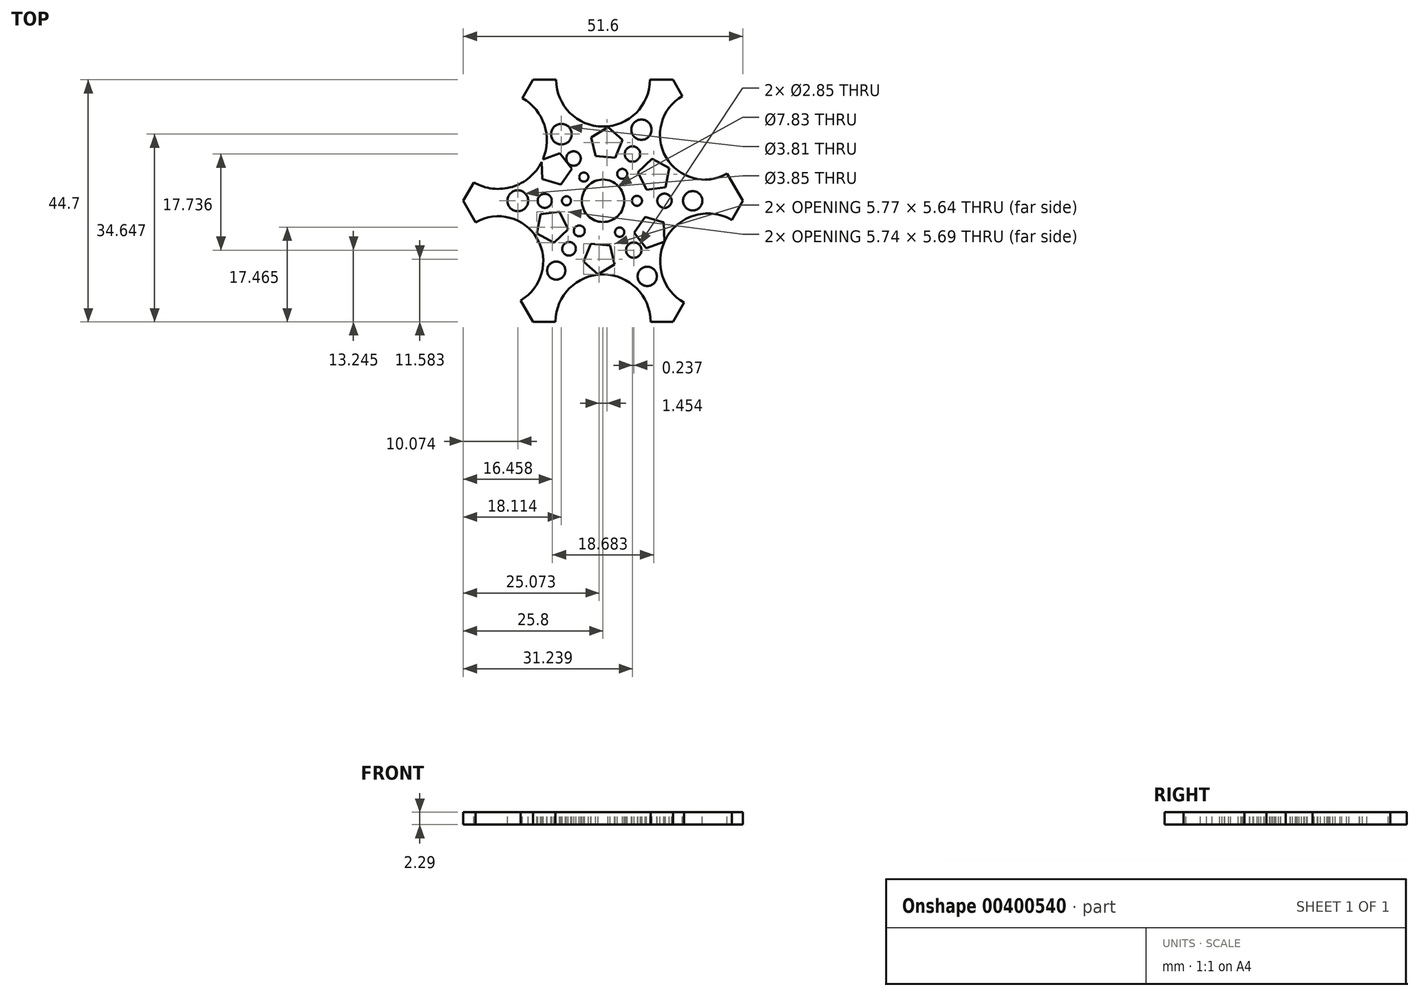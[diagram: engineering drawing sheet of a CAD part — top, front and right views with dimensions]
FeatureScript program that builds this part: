
annotation { "Feature Type Name" : "Feature", "Feature Type Description" : "" }
export const myFeature = defineFeature(function(context is Context, id is Id, definition is map)
    precondition{}
    {
        {
            var Q0;
            Q0=qCreatedBy(makeId("Top.planeOp"),FACE);
            var sketch = newSketch(context, id + "F0", { "sketchPlane" : qUnion([Q0])});
            skCircle(sketch, "E0.cCircle", {"center": v(0, 0) * mm, "radius": 37.25 * mm, "construction": true});
            skLineSegment(sketch, "E0.0", {"start": v(-21.5, 37.25) * mm, "end": v(21.5, 37.25) * mm});
            skLineSegment(sketch, "E0.1", {"start": v(21.5, 37.25) * mm, "end": v(43, 0) * mm});
            skLineSegment(sketch, "E0.2", {"start": v(43, 0) * mm, "end": v(21.5, -37.25) * mm});
            skLineSegment(sketch, "E0.3", {"start": v(21.5, -37.25) * mm, "end": v(-21.5, -37.25) * mm});
            skLineSegment(sketch, "E0.4", {"start": v(-21.5, -37.25) * mm, "end": v(-43, 0) * mm});
            skLineSegment(sketch, "E0.5", {"start": v(-43, 0) * mm, "end": v(-21.5, 37.25) * mm});
            skPoint(sketch, "E0.0.midPoint", {"position": v(0, 37.25) * mm});
            skSolve(sketch);
        }
        {
            var Q0;
            Q0 = qSketchRegion(id + "F0", true);
            extrude(context, id + "F1", {"entities" : qUnion([Q0]), "depth" : 3.8 * mm});
        }
        {
            var Q0;
            Q0=makeQuery(id+"F1.opExtrude","CAP_FACE",FACE,{"disambiguationData":[OSD([sQuery(id+"F0.wireOp",EDGE,"E0.0"),sQuery(id+"F0.wireOp",EDGE,"E0.1"),sQuery(id+"F0.wireOp",EDGE,"E0.2"),sQuery(id+"F0.wireOp",EDGE,"E0.3"),sQuery(id+"F0.wireOp",EDGE,"E0.4"),sQuery(id+"F0.wireOp",EDGE,"E0.5")])],"isStart":false});
            var sketch = newSketch(context, id + "F2", { "sketchPlane" : qUnion([Q0])});
            skCircle(sketch, "E1", {"center": v(0, 37.25) * mm, "radius": 14.42 * mm});
            skCircle(sketch, "E2", {"center": v(-32.26, 18.62) * mm, "radius": 14.97 * mm});
            skCircle(sketch, "E3", {"center": v(-32.26, -18.62) * mm, "radius": 13.87 * mm});
            skCircle(sketch, "E4", {"center": v(0, -37.25) * mm, "radius": 14.61 * mm});
            skCircle(sketch, "E5", {"center": v(32.26, -18.62) * mm, "radius": 14.69 * mm});
            skCircle(sketch, "E6", {"center": v(31.3, 20.28) * mm, "radius": 13.77 * mm});
            skCircle(sketch, "E7", {"center": v(0, 0) * mm, "radius": 6.53 * mm});
            skCircle(sketch, "E8", {"center": v(-12.8, 20.5) * mm, "radius": 3.18 * mm});
            skCircle(sketch, "E9", {"center": v(-9.07, 13) * mm, "radius": 2.23 * mm});
            skCircle(sketch, "E10", {"center": v(-5.91, 7.3) * mm, "radius": 1.4 * mm});
            skCircle(sketch, "E11", {"center": v(11.82, 21.87) * mm, "radius": 3.12 * mm});
            skCircle(sketch, "E12", {"center": v(9.07, 14.39) * mm, "radius": 2.37 * mm});
            skCircle(sketch, "E13", {"center": v(5.91, 8.28) * mm, "radius": 1.54 * mm});
            skCircle(sketch, "E14", {"center": v(27.59, 0) * mm, "radius": 2.96 * mm});
            skCircle(sketch, "E15", {"center": v(18.92, 0) * mm, "radius": 2.2 * mm});
            skCircle(sketch, "E16", {"center": v(13.6, -23.25) * mm, "radius": 2.96 * mm});
            skCircle(sketch, "E17", {"center": v(9.46, -15.17) * mm, "radius": 2.37 * mm});
            skCircle(sketch, "E18", {"center": v(5.12, -9.66) * mm, "radius": 1.43 * mm});
            skCircle(sketch, "E19", {"center": v(10.44, 0) * mm, "radius": 1.54 * mm});
            skCircle(sketch, "E20", {"center": v(-14.39, -21.48) * mm, "radius": 2.8 * mm});
            skCircle(sketch, "E21", {"center": v(-10.44, -14.78) * mm, "radius": 2.1 * mm});
            skCircle(sketch, "E22", {"center": v(-7.3, -9.26) * mm, "radius": 1.67 * mm});
            skCircle(sketch, "E23", {"center": v(-26.21, 0) * mm, "radius": 3.2 * mm});
            skCircle(sketch, "E24", {"center": v(-17.93, 0) * mm, "radius": 2.17 * mm});
            skCircle(sketch, "E25", {"center": v(-11.23, 0) * mm, "radius": 1.4 * mm});
            skSolve(sketch);
        }
        {
            var Q0;
            Q0 = qSketchRegion(id + "F2", true);
            extrude(context, id + "F3", {"entities" : qUnion([Q0]), "operationType" : NewBodyOperationType.REMOVE, "endBound" : BoundingType.THROUGH_ALL, "oppositeDirection" : true, "depth" : 25.4 * mm});
        }
        {
            var Q0;
            Q0=makeQuery(id+"F1.opExtrude","SWEPT_BODY",BODY,{"disambiguationData":[OSD([sQuery(id+"F0.wireOp",EDGE,"E0.0"),sQuery(id+"F0.wireOp",EDGE,"E0.1"),sQuery(id+"F0.wireOp",EDGE,"E0.2"),sQuery(id+"F0.wireOp",EDGE,"E0.3"),sQuery(id+"F0.wireOp",EDGE,"E0.4"),sQuery(id+"F0.wireOp",EDGE,"E0.5")])]});
            var Q1;
            Q1=qCreatedBy(makeId("Origin.pointOp"),VERTEX);
            transform(context, id + "F4", {"entities" : qUnion([Q0]), "transformType" : TransformType.SCALE_UNIFORMLY, "scale" : 0.6, "scalePoint" : qUnion([Q1]), "makeCopy" : false});
        }
        {
            var Q0;
            Q0=makeQuery(id+"F1.opExtrude","CAP_FACE",FACE,{"disambiguationData":[OSD([sQuery(id+"F0.wireOp",EDGE,"E0.0"),sQuery(id+"F0.wireOp",EDGE,"E0.1"),sQuery(id+"F0.wireOp",EDGE,"E0.2"),sQuery(id+"F0.wireOp",EDGE,"E0.3"),sQuery(id+"F0.wireOp",EDGE,"E0.4"),sQuery(id+"F0.wireOp",EDGE,"E0.5")])],"isStart":false});
            var sketch = newSketch(context, id + "F5", { "sketchPlane" : qUnion([Q0])});
            skCircle(sketch, "E26.cCircle", {"center": v(-9.46, -4.71) * mm, "radius": 2.46 * mm, "construction": true});
            skLineSegment(sketch, "E26.0", {"start": v(-8, -2.04) * mm, "end": v(-6.47, -5.27) * mm});
            skLineSegment(sketch, "E26.1", {"start": v(-6.47, -5.27) * mm, "end": v(-9.07, -7.73) * mm});
            skLineSegment(sketch, "E26.2", {"start": v(-9.07, -7.73) * mm, "end": v(-12.21, -6.02) * mm});
            skLineSegment(sketch, "E26.3", {"start": v(-12.21, -6.02) * mm, "end": v(-11.55, -2.5) * mm});
            skLineSegment(sketch, "E26.4", {"start": v(-11.55, -2.5) * mm, "end": v(-8, -2.04) * mm});
            skPoint(sketch, "E26.0.midPoint", {"position": v(-7.24, -3.66) * mm});
            skLineSegment(sketch, "E27.1.0", {"start": v(-3.61, -11.25) * mm, "end": v(-2.23, -7.95) * mm});
            skPoint(sketch, "E27.1.1", {"position": v(-0.45, -8.1) * mm});
            skLineSegment(sketch, "E27.1.2", {"start": v(-0.9, -13.59) * mm, "end": v(-3.61, -11.25) * mm});
            skLineSegment(sketch, "E27.1.3", {"start": v(2.16, -11.72) * mm, "end": v(-0.9, -13.59) * mm});
            skLineSegment(sketch, "E27.1.4", {"start": v(1.33, -8.24) * mm, "end": v(2.16, -11.72) * mm});
            skCircle(sketch, "E27.1.5", {"center": v(-0.65, -10.55) * mm, "radius": 2.46 * mm, "construction": true});
            skLineSegment(sketch, "E27.1.6", {"start": v(-2.23, -7.95) * mm, "end": v(1.33, -8.24) * mm});
            skLineSegment(sketch, "E27.2.0", {"start": v(7.94, -8.76) * mm, "end": v(5.77, -5.91) * mm});
            skPoint(sketch, "E27.2.1", {"position": v(6.78, -4.44) * mm});
            skLineSegment(sketch, "E27.2.2", {"start": v(11.32, -7.57) * mm, "end": v(7.94, -8.76) * mm});
            skLineSegment(sketch, "E27.2.3", {"start": v(11.23, -4) * mm, "end": v(11.32, -7.57) * mm});
            skLineSegment(sketch, "E27.2.4", {"start": v(7.8, -2.97) * mm, "end": v(11.23, -4) * mm});
            skCircle(sketch, "E27.2.5", {"center": v(8.81, -5.84) * mm, "radius": 2.46 * mm, "construction": true});
            skLineSegment(sketch, "E27.2.6", {"start": v(5.77, -5.91) * mm, "end": v(7.8, -2.97) * mm});
            skLineSegment(sketch, "E27.3.0", {"start": v(11.55, 2.5) * mm, "end": v(8, 2.04) * mm});
            skPoint(sketch, "E27.3.1", {"position": v(7.24, 3.66) * mm});
            skLineSegment(sketch, "E27.3.2", {"start": v(12.21, 6.02) * mm, "end": v(11.55, 2.5) * mm});
            skLineSegment(sketch, "E27.3.3", {"start": v(9.07, 7.73) * mm, "end": v(12.21, 6.02) * mm});
            skLineSegment(sketch, "E27.3.4", {"start": v(6.47, 5.27) * mm, "end": v(9.07, 7.73) * mm});
            skCircle(sketch, "E27.3.5", {"center": v(9.46, 4.71) * mm, "radius": 2.46 * mm, "construction": true});
            skLineSegment(sketch, "E27.3.6", {"start": v(8, 2.04) * mm, "end": v(6.47, 5.27) * mm});
            skLineSegment(sketch, "E27.4.0", {"start": v(3.61, 11.25) * mm, "end": v(2.23, 7.95) * mm});
            skPoint(sketch, "E27.4.1", {"position": v(0.45, 8.1) * mm});
            skLineSegment(sketch, "E27.4.2", {"start": v(0.9, 13.59) * mm, "end": v(3.61, 11.25) * mm});
            skLineSegment(sketch, "E27.4.3", {"start": v(-2.16, 11.72) * mm, "end": v(0.9, 13.59) * mm});
            skLineSegment(sketch, "E27.4.4", {"start": v(-1.33, 8.24) * mm, "end": v(-2.16, 11.72) * mm});
            skCircle(sketch, "E27.4.5", {"center": v(0.65, 10.55) * mm, "radius": 2.46 * mm, "construction": true});
            skLineSegment(sketch, "E27.4.6", {"start": v(2.23, 7.95) * mm, "end": v(-1.33, 8.24) * mm});
            skLineSegment(sketch, "E27.5.0", {"start": v(-7.94, 8.76) * mm, "end": v(-5.77, 5.91) * mm});
            skPoint(sketch, "E27.5.1", {"position": v(-6.78, 4.44) * mm});
            skLineSegment(sketch, "E27.5.2", {"start": v(-11.32, 7.57) * mm, "end": v(-7.94, 8.76) * mm});
            skLineSegment(sketch, "E27.5.3", {"start": v(-11.23, 4) * mm, "end": v(-11.32, 7.57) * mm});
            skLineSegment(sketch, "E27.5.4", {"start": v(-7.8, 2.97) * mm, "end": v(-11.23, 4) * mm});
            skCircle(sketch, "E27.5.5", {"center": v(-8.81, 5.84) * mm, "radius": 2.46 * mm, "construction": true});
            skLineSegment(sketch, "E27.5.6", {"start": v(-5.77, 5.91) * mm, "end": v(-7.8, 2.97) * mm});
            skPoint(sketch, "E27.center", {"position": v(0, 0) * mm});
            skSolve(sketch);
        }
        {
            var Q0;
            Q0=makeQuery(id+"F5.imprint","IMPRINT",FACE,{"disambiguationData":[TD([[makeQuery(id+"F5.imprint","IMPRINT",EDGE,{"derivedFrom":sQuery(id+"F5.wireOp",EDGE,"E27.4.0")}),-1.0]])]});
            var Q1;
            {var subQ5=sQuery(id+"F5.wireOp",EDGE,"E27.5.0");Q1=makeQuery(id+"F5.imprint","IMPRINT",FACE,{"disambiguationData":[TD([[makeQuery(id+"F5.imprint","IMPRINT",EDGE,{"derivedFrom":subQ5}),-1.0]])]});}
            var Q2;
            Q2=makeQuery(id+"F5.imprint","IMPRINT",FACE,{"disambiguationData":[TD([[makeQuery(id+"F5.imprint","IMPRINT",EDGE,{"derivedFrom":sQuery(id+"F5.wireOp",EDGE,"E26.0")}),-1.0]])]});
            var Q3;
            Q3=makeQuery(id+"F5.imprint","IMPRINT",FACE,{"disambiguationData":[TD([[makeQuery(id+"F5.imprint","IMPRINT",EDGE,{"derivedFrom":sQuery(id+"F5.wireOp",EDGE,"E27.1.0")}),-1.0]])]});
            var Q4;
            {var subQ5=sQuery(id+"F5.wireOp",EDGE,"E27.2.0");Q4=makeQuery(id+"F5.imprint","IMPRINT",FACE,{"disambiguationData":[TD([[makeQuery(id+"F5.imprint","IMPRINT",EDGE,{"derivedFrom":subQ5}),-1.0]])]});}
            var Q5;
            Q5=makeQuery(id+"F5.imprint","IMPRINT",FACE,{"disambiguationData":[TD([[makeQuery(id+"F5.imprint","IMPRINT",EDGE,{"derivedFrom":sQuery(id+"F5.wireOp",EDGE,"E27.3.0")}),-1.0]])]});
            extrude(context, id + "F6", {"entities" : qUnion([Q0, Q1, Q2, Q3, Q4, Q5]), "operationType" : NewBodyOperationType.REMOVE, "endBound" : BoundingType.THROUGH_ALL, "oppositeDirection" : true, "depth" : 25.4 * mm});
        }
    });
